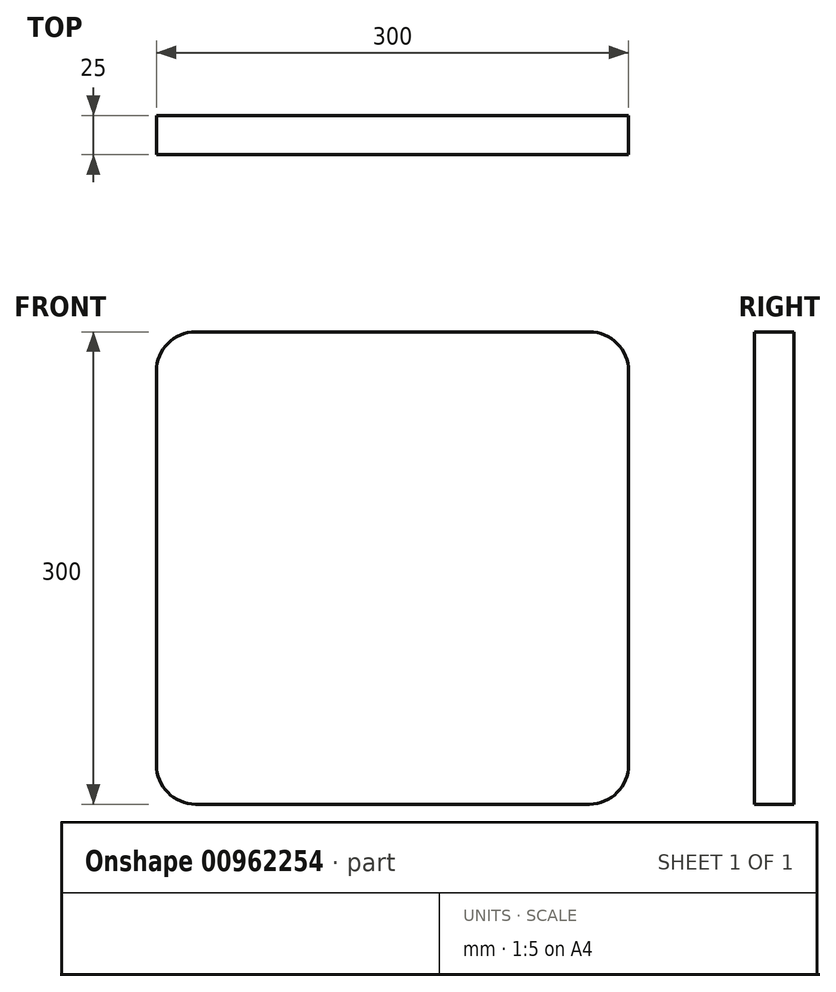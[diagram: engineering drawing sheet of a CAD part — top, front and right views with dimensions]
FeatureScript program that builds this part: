
annotation { "Feature Type Name" : "Feature", "Feature Type Description" : "" }
export const myFeature = defineFeature(function(context is Context, id is Id, definition is map)
    precondition{}
    {
        {
            var Q0;
            Q0=qCreatedBy(makeId("Front.planeOp"),FACE);
            var sketch = newSketch(context, id + "F0", { "sketchPlane" : qUnion([Q0])});
            skLineSegment(sketch, "E0.bottom", {"start": v(25, 0) * mm, "end": v(275, 0) * mm});
            skLineSegment(sketch, "E0.top", {"start": v(25, 300) * mm, "end": v(275, 300) * mm});
            skLineSegment(sketch, "E0.left", {"start": v(0, 25) * mm, "end": v(0, 275) * mm});
            skLineSegment(sketch, "E0.right", {"start": v(300, 25) * mm, "end": v(300, 275) * mm});
            skPoint(sketch, "E1.visualSharp", {"position": v(0, 300) * mm});
            skArc(sketch, "E1.filletArc", {"start": v(25, 300) * mm, "mid": v(7.32, 292.68) * mm, "end": v(0, 275) * mm});
            skPoint(sketch, "E2.visualSharp", {"position": v(300, 300) * mm});
            skArc(sketch, "E2.filletArc", {"start": v(300, 275) * mm, "mid": v(292.68, 292.68) * mm, "end": v(275, 300) * mm});
            skPoint(sketch, "E3.visualSharp", {"position": v(300, 0) * mm});
            skArc(sketch, "E3.filletArc", {"start": v(275, 0) * mm, "mid": v(292.68, 7.32) * mm, "end": v(300, 25) * mm});
            skPoint(sketch, "E4.visualSharp", {"position": v(0, 0) * mm});
            skArc(sketch, "E4.filletArc", {"start": v(0, 25) * mm, "mid": v(7.32, 7.32) * mm, "end": v(25, 0) * mm});
            skSolve(sketch);
        }
        {
            var Q0;
            Q0=makeQuery(id+"F0.imprint","IMPRINT",FACE,{"disambiguationData":[TD([[makeQuery(id+"F0.imprint","IMPRINT",EDGE,{"derivedFrom":sQuery(id+"F0.wireOp",EDGE,"E0.bottom")}),1.0]])]});
            extrude(context, id + "F1", {"entities" : qUnion([Q0]), "depth" : 25 * mm, "offsetDistance" : 25 * mm});
        }
    });
